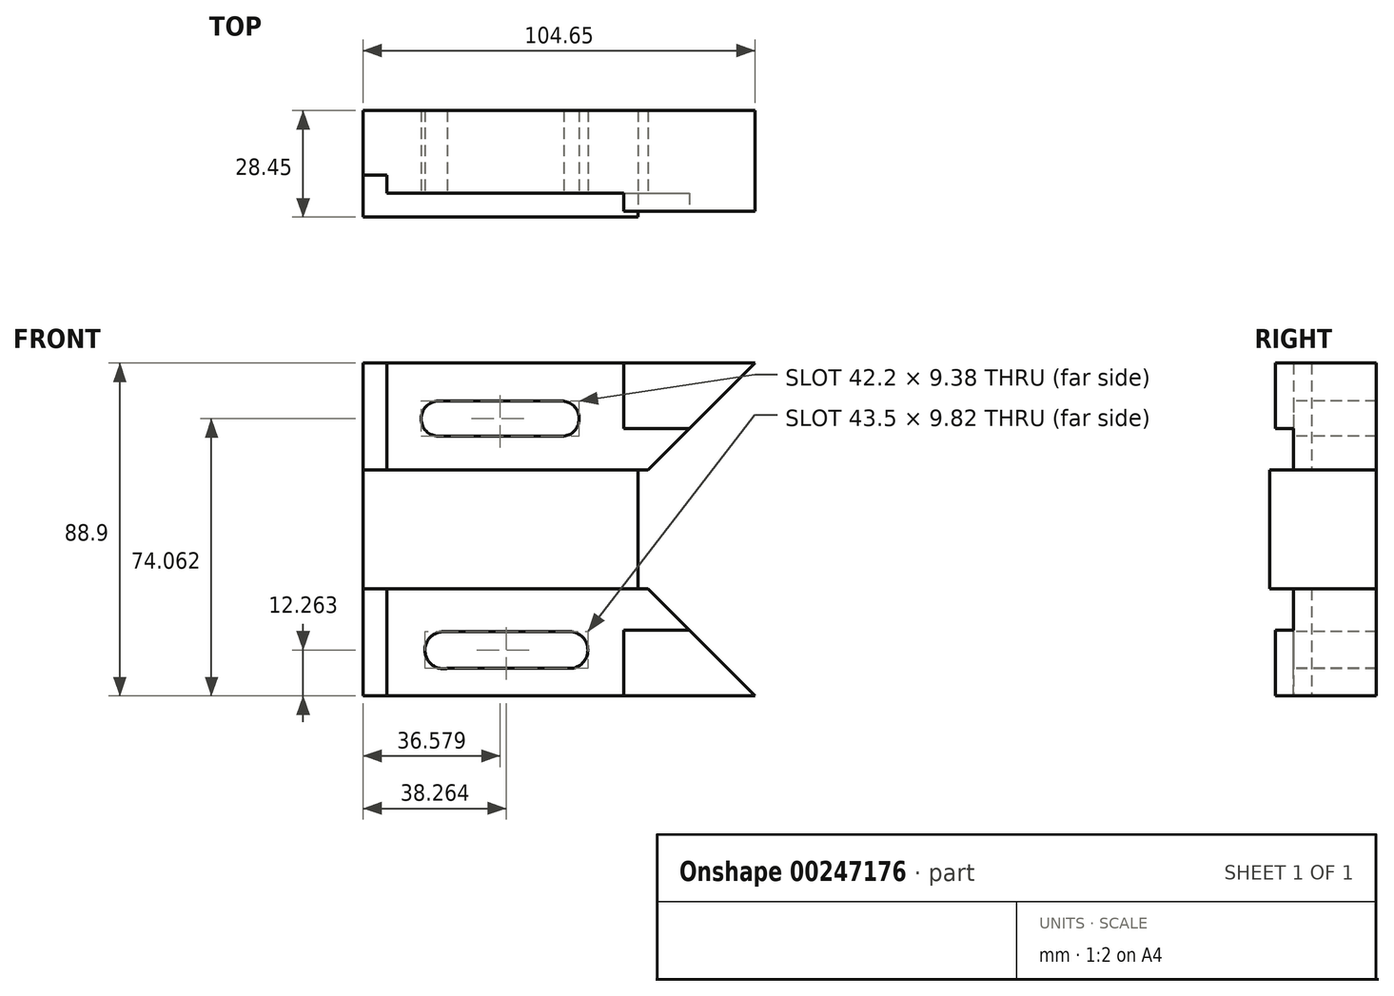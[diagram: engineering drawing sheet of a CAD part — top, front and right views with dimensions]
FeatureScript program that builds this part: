
annotation { "Feature Type Name" : "Feature", "Feature Type Description" : "" }
export const myFeature = defineFeature(function(context is Context, id is Id, definition is map)
    precondition{}
    {
        {
            var Q0;
            Q0=qCreatedBy(makeId("Front.planeOp"),FACE);
            var sketch = newSketch(context, id + "F0", { "sketchPlane" : qUnion([Q0])});
            skLineSegment(sketch, "E0.bottom", {"start": v(-64.38, 28.58) * mm, "end": v(40.27, 28.58) * mm});
            skLineSegment(sketch, "E0.top", {"start": v(-64.38, -60.32) * mm, "end": v(40.27, -60.32) * mm});
            skLineSegment(sketch, "E0.left", {"start": v(-64.38, 28.58) * mm, "end": v(-64.38, -60.32) * mm});
            skLineSegment(sketch, "E1", {"start": v(-64.38, 0) * mm, "end": v(11.7, 0) * mm});
            skLineSegment(sketch, "E2", {"start": v(11.7, 0) * mm, "end": v(40.27, 28.58) * mm});
            skLineSegment(sketch, "E3", {"start": v(-64.38, -31.75) * mm, "end": v(11.7, -31.75) * mm});
            skLineSegment(sketch, "E4", {"start": v(11.7, -31.75) * mm, "end": v(40.27, -60.32) * mm});
            skLineSegment(sketch, "E5", {"start": v(9.03, 0) * mm, "end": v(9.03, -31.75) * mm});
            skLineSegment(sketch, "E6", {"start": v(5.22, 28.58) * mm, "end": v(5.22, 11.05) * mm});
            skLineSegment(sketch, "E7", {"start": v(5.22, 11.05) * mm, "end": v(22.75, 11.05) * mm});
            skLineSegment(sketch, "E8", {"start": v(5.22, -60.32) * mm, "end": v(5.22, -42.8) * mm});
            skLineSegment(sketch, "E9", {"start": v(5.22, -42.8) * mm, "end": v(22.75, -42.8) * mm});
            skLineSegment(sketch, "E10", {"start": v(-58.03, 28.58) * mm, "end": v(-58.03, 0) * mm});
            skLineSegment(sketch, "E11", {"start": v(-58.03, -31.75) * mm, "end": v(-58.03, -60.32) * mm});
            skLineSegment(sketch, "E12", {"start": v(-44.21, 18.43) * mm, "end": v(-11.4, 18.43) * mm});
            skLineSegment(sketch, "E13", {"start": v(-44.21, 9.05) * mm, "end": v(-10.76, 9.05) * mm});
            skLineSegment(sketch, "E14", {"start": v(-42.93, -43.15) * mm, "end": v(-9.27, -43.15) * mm});
            skLineSegment(sketch, "E15", {"start": v(-9.27, -52.95) * mm, "end": v(-41.87, -52.95) * mm});
            skArc(sketch, "E16", {"start": v(-44.21, 18.43) * mm, "mid": v(-48.9, 13.74) * mm, "end": v(-44.21, 9.05) * mm});
            skArc(sketch, "E17", {"start": v(-10.76, 9.05) * mm, "mid": v(-6.7, 14.04) * mm, "end": v(-11.4, 18.43) * mm});
            skArc(sketch, "E18", {"start": v(-42.93, -43.15) * mm, "mid": v(-47.86, -48.64) * mm, "end": v(-41.87, -52.95) * mm});
            skArc(sketch, "E19", {"start": v(-9.27, -52.95) * mm, "mid": v(-4.37, -48.05) * mm, "end": v(-9.27, -43.15) * mm});
            skSolve(sketch);
        }
        {
            var Q0;
            Q0 = qSketchRegion(id + "F0", true);
            extrude(context, id + "F1", {"entities" : qUnion([Q0]), "oppositeDirection" : true, "depth" : 28.45 * mm});
        }
        {
            var Q0;
            {var subQ6=sQuery(id+"F0.wireOp",EDGE,"E6");Q0=makeQuery(id+"F0.imprint","IMPRINT",FACE,{"disambiguationData":[TD([[makeQuery(id+"F0.imprint","IMPRINT",EDGE,{"derivedFrom":subQ6}),-1.0]])]});}
            extrude(context, id + "F2", {"entities" : qUnion([Q0]), "operationType" : NewBodyOperationType.REMOVE, "depth" : 6.35 * mm});
        }
        {
            var Q0;
            {var subQ6=sQuery(id+"F0.wireOp",EDGE,"E8");Q0=makeQuery(id+"F0.imprint","IMPRINT",FACE,{"disambiguationData":[TD([[makeQuery(id+"F0.imprint","IMPRINT",EDGE,{"derivedFrom":subQ6}),1.0]])]});}
            extrude(context, id + "F3", {"entities" : qUnion([Q0]), "operationType" : NewBodyOperationType.REMOVE, "depth" : 6.35 * mm});
        }
        {
            var Q0;
            {var subQ6=sQuery(id+"F0.wireOp",EDGE,"E6");Q0=makeQuery(id+"F0.imprint","IMPRINT",FACE,{"disambiguationData":[TD([[makeQuery(id+"F0.imprint","IMPRINT",EDGE,{"derivedFrom":subQ6}),-1.0]])]});}
            extrude(context, id + "F4", {"entities" : qUnion([Q0]), "operationType" : NewBodyOperationType.REMOVE, "oppositeDirection" : true, "depth" : 6.35 * mm});
        }
        {
            var Q0;
            {var subQ6=sQuery(id+"F0.wireOp",EDGE,"E6");Q0=makeQuery(id+"F0.imprint","IMPRINT",FACE,{"disambiguationData":[TD([[makeQuery(id+"F0.imprint","IMPRINT",EDGE,{"derivedFrom":subQ6}),-1.0]])]});}
            var Q1;
            {var subQ6=sQuery(id+"F0.wireOp",EDGE,"E8");Q1=makeQuery(id+"F0.imprint","IMPRINT",FACE,{"disambiguationData":[TD([[makeQuery(id+"F0.imprint","IMPRINT",EDGE,{"derivedFrom":subQ6}),1.0]])]});}
            var Q2;
            Q2=sQuery(id+"F0.wireOp",EDGE,"E10");
            var Q3;
            Q3=sQuery(id+"F0.wireOp",EDGE,"E1");
            var Q4;
            Q4=sQuery(id+"F0.wireOp",EDGE,"E7");
            var Q5;
            Q5=sQuery(id+"F0.wireOp",EDGE,"E6");
            var Q6;
            Q6=sQuery(id+"F0.wireOp",EDGE,"E0.bottom");
            extrude(context, id + "F5", {"entities" : qUnion([Q0, Q1]), "operationType" : NewBodyOperationType.REMOVE, "surfaceEntities" : qUnion([Q2, Q3, Q4, Q5, Q6]), "endBound" : BoundingType.SYMMETRIC, "oppositeDirection" : true, "depth" : 11.18 * mm});
        }
        {
            var Q0;
            {var subQ6=sQuery(id+"F0.wireOp",EDGE,"E6");Q0=makeQuery(id+"F0.imprint","IMPRINT",FACE,{"disambiguationData":[TD([[makeQuery(id+"F0.imprint","IMPRINT",EDGE,{"derivedFrom":subQ6}),-1.0]])]});}
            var Q1;
            {var subQ6=sQuery(id+"F0.wireOp",EDGE,"E8");Q1=makeQuery(id+"F0.imprint","IMPRINT",FACE,{"disambiguationData":[TD([[makeQuery(id+"F0.imprint","IMPRINT",EDGE,{"derivedFrom":subQ6}),1.0]])]});}
            extrude(context, id + "F6", {"entities" : qUnion([Q0, Q1]), "operationType" : NewBodyOperationType.REMOVE, "oppositeDirection" : true, "depth" : 6.35 * mm});
        }
        {
            var Q0;
            {var subQ3=sQuery(id+"F0.wireOp",EDGE,"E10");Q0=makeQuery(id+"F0.imprint","IMPRINT",FACE,{"disambiguationData":[TD([[makeQuery(id+"F0.imprint","IMPRINT",EDGE,{"derivedFrom":subQ3}),-1.0]])]});}
            var Q1;
            {var subQ3=sQuery(id+"F0.wireOp",EDGE,"E11");Q1=makeQuery(id+"F0.imprint","IMPRINT",FACE,{"disambiguationData":[TD([[makeQuery(id+"F0.imprint","IMPRINT",EDGE,{"derivedFrom":subQ3}),-1.0]])]});}
            extrude(context, id + "F7", {"entities" : qUnion([Q0, Q1]), "operationType" : NewBodyOperationType.REMOVE, "oppositeDirection" : true, "depth" : 11.18 * mm});
        }
        {
            var Q0;
            {var subQ3=sQuery(id+"F0.wireOp",EDGE,"E6");Q0=makeQuery(id+"F0.imprint","IMPRINT",FACE,{"disambiguationData":[TD([[makeQuery(id+"F0.imprint","IMPRINT",EDGE,{"derivedFrom":subQ3}),1.0]])]});}
            var Q1;
            {var subQ3=sQuery(id+"F0.wireOp",EDGE,"E8");Q1=makeQuery(id+"F0.imprint","IMPRINT",FACE,{"disambiguationData":[TD([[makeQuery(id+"F0.imprint","IMPRINT",EDGE,{"derivedFrom":subQ3}),-1.0]])]});}
            extrude(context, id + "F8", {"entities" : qUnion([Q0, Q1]), "operationType" : NewBodyOperationType.REMOVE, "oppositeDirection" : true, "depth" : 1.52 * mm});
        }
        {
            var Q0;
            Q0=qCreatedBy(makeId("Front.planeOp"),FACE);
            cPlane(context, id + "F9", {"entities" : qUnion([Q0]), "cplaneType" : CPlaneType.OFFSET, "offset" : 28.7 * mm, "oppositeDirection" : true, "width" : 152.4 * mm, "height" : 152.4 * mm});
        }
    });
